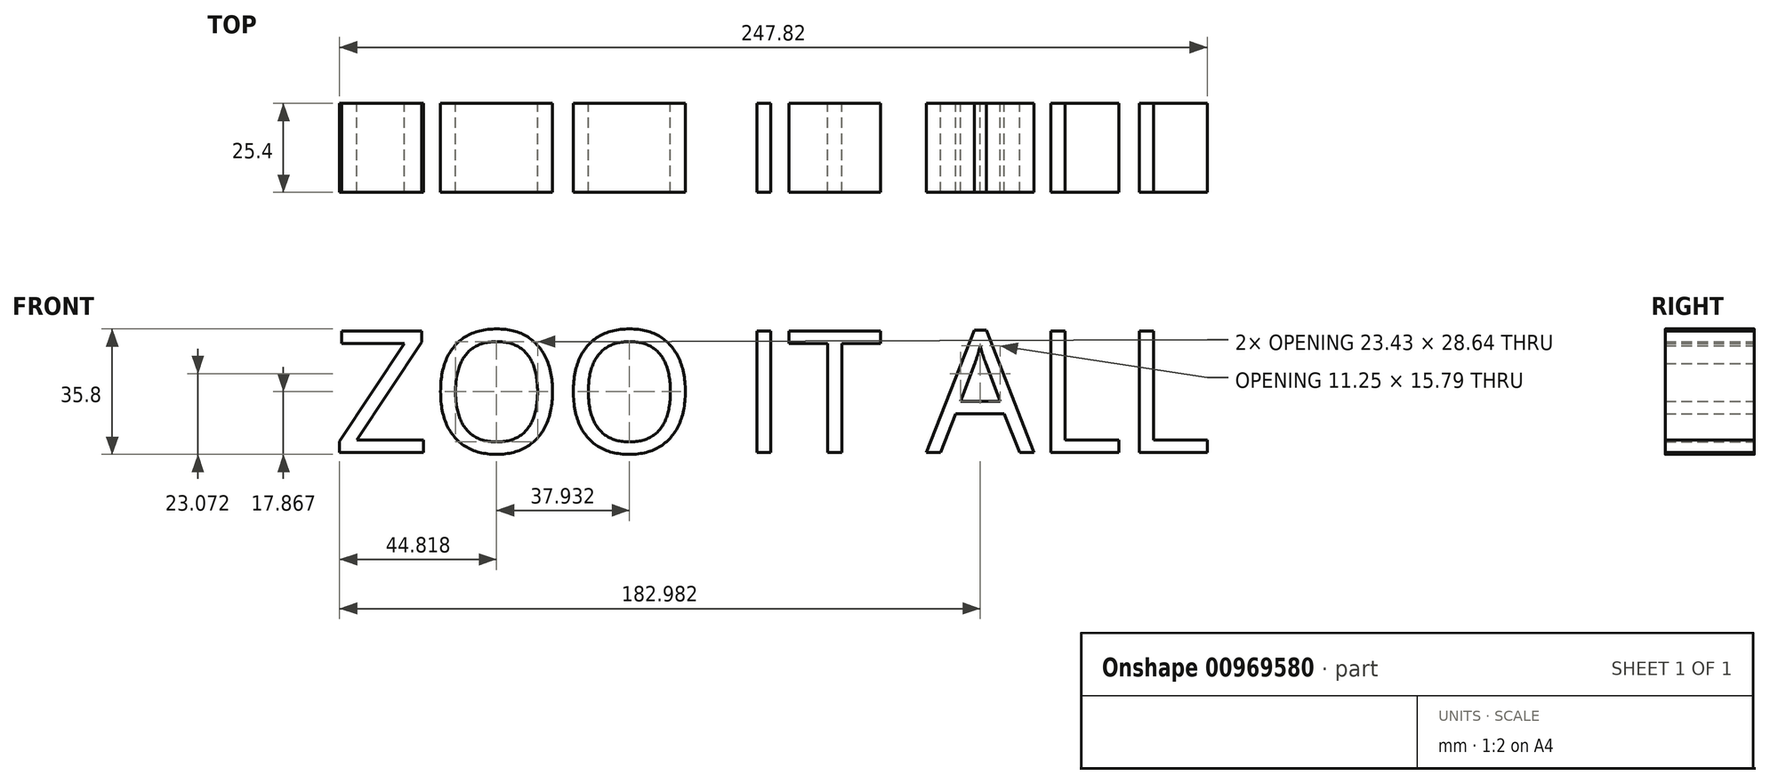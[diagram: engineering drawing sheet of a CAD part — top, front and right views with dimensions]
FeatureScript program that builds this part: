
annotation { "Feature Type Name" : "Feature", "Feature Type Description" : "" }
export const myFeature = defineFeature(function(context is Context, id is Id, definition is map)
    precondition{}
    {
        {
            var Q0;
            Q0=qCreatedBy(makeId("Front.planeOp"),FACE);
            var sketch = newSketch(context, id + "F0", { "sketchPlane" : qUnion([Q0])});
            skText(sketch, "E0", { "text": "ZOO IT ALL", "fontName": "OpenSans-Regular.ttf"});
            const initialGuessF0  = {"E0": [-0.11214, -0.0265, 1, 0, 0.03507]};
            skSetInitialGuess(sketch, initialGuessF0);
            skSolve(sketch);
        }
        {
            var Q0;
            Q0 = qSketchRegion(id + "F0", true);
            extrude(context, id + "F1", {"entities" : qUnion([Q0]), "depth" : 25.4 * mm, "offsetDistance" : 25.4 * mm});
        }
    });
